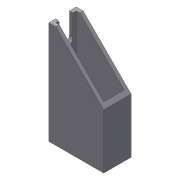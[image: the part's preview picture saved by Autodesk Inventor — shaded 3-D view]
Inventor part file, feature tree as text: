
AUTODESK INVENTOR PART (.ipt)
format: ipt  version: 2012 (Build 160160000, 160)  size: 109,568 bytes
history: native  units: in
note: dims shown in document units (in); Inventor stores cm internally (conversion verified against a paired STEP export)
features: extrude x4, sketch x4, shell x1, chamfer x1
ambient origin geometry x8: Origin, YZ Plane, XZ Plane, XY Plane, X Axis, Y Axis, Z Axis, Center Point
bodies: Solid1 (feature_tree)
feature tree (10):
  extrude  "Extrusion1"  Depth=0.125in
  shell  "Shell1"  Thickness=2.0in
  extrude  "Extrusion2"  Depth=2.0in
  extrude  "Extrusion3"  Depth=1.0in
  chamfer  "Chamfer1"  Distance=0.5in
  extrude  "Extrusion4"  Depth=1.0in TaperAngle=0.0deg
  sketch  "Sketch1"  dims[d0=1.0in d1=0.0in d2=0.125in d3=2.0in]
  sketch  "Sketch2"  dims[d4=4.0in d5=2.0in]
  sketch  "Sketch3"  dims[d6=1.0in d7=0.0in d8=1.0in]
  sketch  "Sketch4"  dims[d9=0.25in d10=0.5in d11=1.0in d12=0.0in d13=0.125in d14=0.125in d15=45.0deg d16=0.25in d17=1.0in d18=0.0in]
